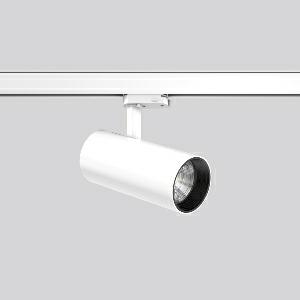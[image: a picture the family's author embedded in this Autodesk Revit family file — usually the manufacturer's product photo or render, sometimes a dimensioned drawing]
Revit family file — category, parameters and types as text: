
# Revit family: deecos_s_mini_742207_002_48a3
name_source: partatom
category: Lighting Fixtures
units: mm (PartAtom-declared; Revit-internal decimal feet)

## family parameters
Cut with Voids When Loaded = No
Host = Face
Light Source = No
Part Type = Normal
Room Calculation Point = No
Round Connector Dimension = Use Diameter
Shared = No

## types (1)
- DEECOS S mini (1 x LED Modul 930, 3000 lm, 3000)
    Apparent Load = 29 VA
    Approval mark = CE
    CIE Flux Codes = 96 100 100 100 100
    Color Rendering = 90
    Color Temperature = 3000
    Default Elevation = 1800 mm
    Description = Series: DEECOS S mini
LED surface-mounted projector in modern design with no visible cooling ribs. Housing: die-cast aluminium, powder-coated. Rotation range: 356°. Swivel range: 90°. Black plastic ring and recessed LED to prevent glare from the side. Optical assembly with lens made of plastic (polycarbonate) for the best homogeneous light distribution - can be changed without tools. Best colour rendering index Ra>90. With multi adaptor for 3-circuit tracks 230 V. Suitable for Track on ceiling, Wall track. High quality converter without flickering and stroboscopic effect. The following accessories can be mounted without use of tools: interchangeable lenses, decorative glasses, honeycomb louvre, clear and frosted diffusers, white interchangeable plastic ring. 
Colour: traffic white, matt (RAL 9016)
Diameter: 87 mm
Height: 214 mm
Lamp: LED
Socket: without socket
Colour temperature: 3000K
Colour rendering index (CRI): 92
System power: 29 W
Rated luminous flux: 3000 lm
Luminous efficiency: 103 lm/W
Control gear: Regulated power supply
Protection class: I
Type of protection: IP 20
    Height = 214 mm
    Lamp = 1 x LED Modul 930
    Lamp Light Flux = 3000 lm
    Lamp count = 1
    Length = 87 mm
    Lifetime = 50000 h
    Luminous efficacy = 103 lm/W
    Manufacturer = RZB
    ModVariant = No
    Model = 742207.002
    Mounting Place = Ceiling
    Mounting Type = Rail mounted
    Number of Poles = 1
    OnlyDefault = Yes
    Power Factor = 1
    Product Name = DEECOS S mini
    Product group = Track mounted projectors
    ProductGroupID = 301
    Protection Class = Protection class I
    Protection Degree = IP 20
    RLX_Detail_Level = 1
    RLX_Emergency_Light_Flux = 0 lm
    RLX_Emergency_Type = 0
    RLX_Emergency_Type_DB = No
    RlxData = <blob elided: 35661 chars, md5=25870818>
    Socket = socket
    Standby Power = 0 W
    System Light Flux = 3000 lm
    System Power = 29 W
    Type Comments = Product without accessories
    Type Image = 741930.002.jpg
    URL = http://relux.com
    VarID = ---
    Voltage = 230 V
    Voltage Range = 220-240 V
    Weight = 0.00 kg
    Width = 0 mm  [stored 0 ft]

note: [stored X ft] marks values corroborated as IEEE doubles in the binary element streams (Revit-internal decimal feet)

## geometry (parser evidence)
native form markers: Blend x4, Sweep x12
no freeform markers — native parametric forms only
